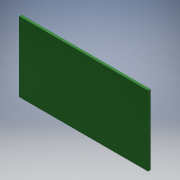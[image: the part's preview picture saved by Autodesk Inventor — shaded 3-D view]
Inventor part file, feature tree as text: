
AUTODESK INVENTOR PART (.ipt)
format: ipt  version: 2018 (Build 220112000, 112)  size: 182,784 bytes
history: native  units: mm
features: extrude x4, sketch x4
ambient origin geometry x8: Origin, YZ Plane, XZ Plane, XY Plane, X Axis, Y Axis, Z Axis, Center Point
bodies: Solid1 (feature_tree)
feature tree (8):
  extrude  "Extrusion1"  Depth=86.95mm
  extrude  "Extrusion4"  Depth=48.0mm
  extrude  "Extrusion5"  Depth=15.3mm
  extrude  "Extrusion6"  Depth=4.1mm
  sketch  "Sketch1"  dims[d0=160.0mm d1=86.95mm]
  sketch  "Sketch2"  dims[d2=3.0mm d3=0.0mm d6=48.0mm]
  sketch  "Sketch4"  dims[d7=20.4mm d26=15.3mm]
  sketch  "Sketch5"  dims[d27=22.1mm d29=4.1mm d30=15.3mm d32=15.3mm d36=12.4mm d37=29.3mm d38=15.3mm d42=15.3mm d44=15.3mm d46=6.1mm d47=6.1mm d48=6.1mm d49=6.1mm d50=6.1mm d51=11.4mm d52=10.4mm d53=17.0mm d54=73.4mm d55=11.7mm d56=10.0mm d57=0.0mm d58=3.0mm d59=0.0mm d60=15.2mm d61=5.6mm d62=27.45mm d63=14.2mm d64=15.2mm d65=5.6mm d66=4.1mm d67=8.5mm d68=0.0mm]
